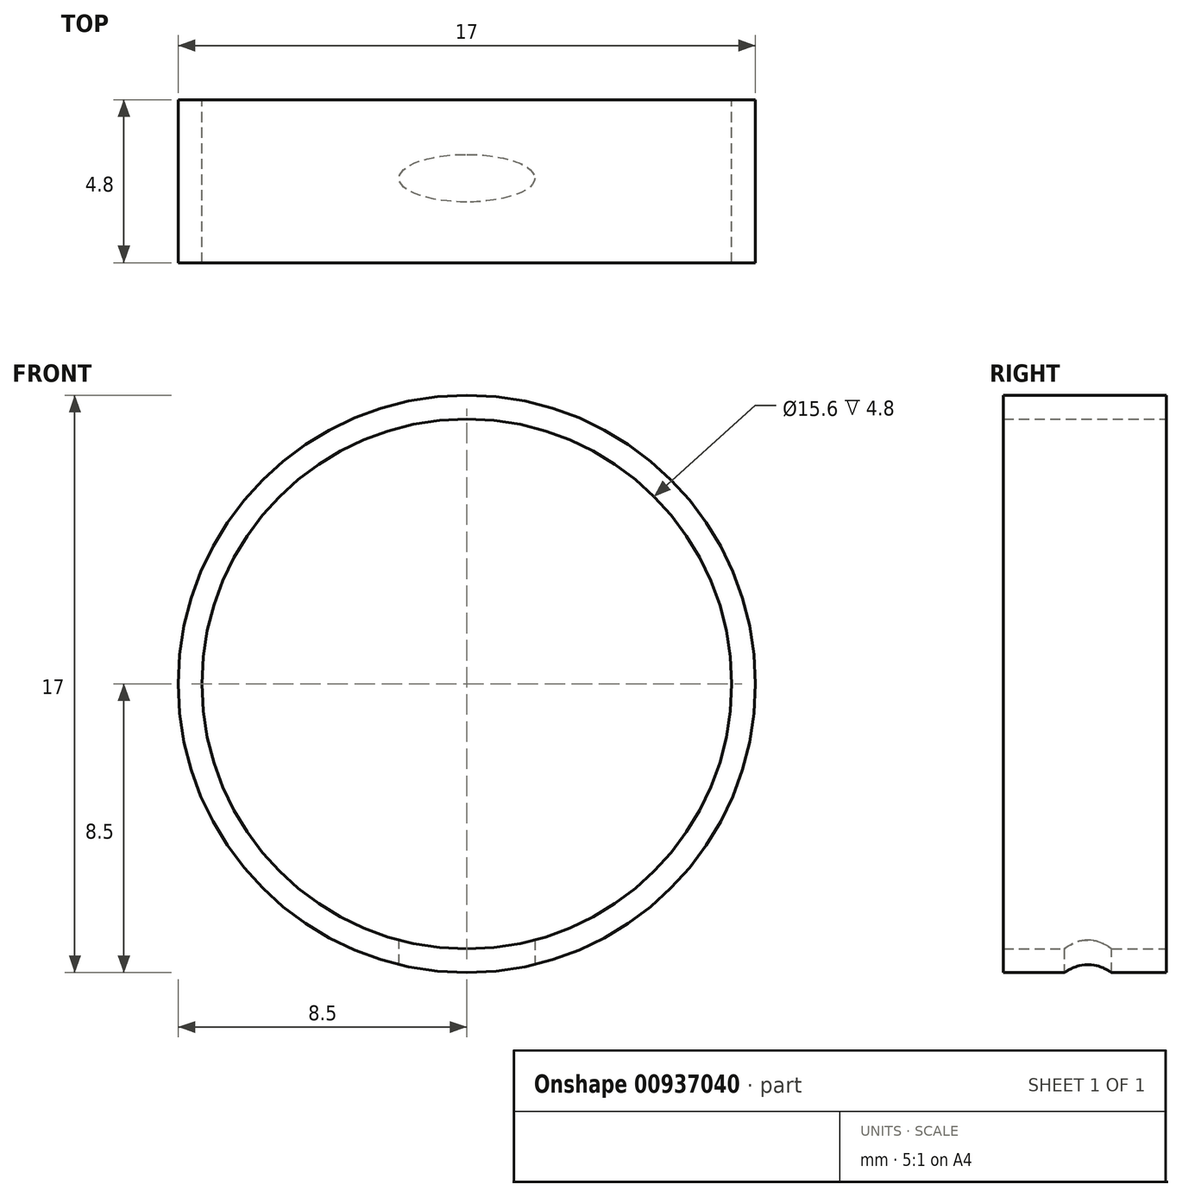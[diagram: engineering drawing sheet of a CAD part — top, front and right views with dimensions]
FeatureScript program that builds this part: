
annotation { "Feature Type Name" : "Feature", "Feature Type Description" : "" }
export const myFeature = defineFeature(function(context is Context, id is Id, definition is map)
    precondition{}
    {
        {
            var Q0;
            Q0=qCreatedBy(makeId("Front.planeOp"),FACE);
            var sketch = newSketch(context, id + "F0", { "sketchPlane" : qUnion([Q0])});
            skCircle(sketch, "E0", {"center": v(0, 0) * mm, "radius": 8.5 * mm});
            skCircle(sketch, "E1", {"center": v(0, 0) * mm, "radius": 7.8 * mm});
            skSolve(sketch);
        }
        {
            var Q0;
            Q0=makeQuery(id+"F0.imprint","IMPRINT",FACE,{"disambiguationData":[TD([[makeQuery(id+"F0.imprint","IMPRINT",EDGE,{"derivedFrom":sQuery(id+"F0.wireOp",EDGE,"E0")}),1.0]])]});
            extrude(context, id + "F1", {"entities" : qUnion([Q0]), "depth" : 4.8 * mm, "offsetDistance" : 25 * mm});
        }
        {
            var Q0;
            Q0=qCreatedBy(makeId("Top.planeOp"),FACE);
            cPlane(context, id + "F2", {"entities" : qUnion([Q0]), "cplaneType" : CPlaneType.OFFSET, "offset" : 9 * mm, "oppositeDirection" : true, "width" : 150 * mm, "height" : 150 * mm});
        }
        {
            var Q0;
            Q0=qCreatedBy(id+"F2.planeOp",FACE);
            var sketch = newSketch(context, id + "F3", { "sketchPlane" : qUnion([Q0])});
            skLineSegment(sketch, "E2.0", {"start": v(8.5, 0) * mm, "end": v(-8.5, 0) * mm});
            skLineSegment(sketch, "E3.0", {"start": v(8.5, -4.8) * mm, "end": v(-8.5, -4.8) * mm});
            skLineSegment(sketch, "E4", {"start": v(8.5, 0) * mm, "end": v(8.5, -4.62) * mm});
            skLineSegment(sketch, "E5", {"start": v(-8.5, -4.62) * mm, "end": v(-8.5, 0) * mm});
            skEllipse(sketch, "E6", {"center": v(0, -2.31) * mm, "majorRadius": 2 * mm, "minorRadius": 0.7 * mm, "majorAxis": v(1, 0)});
            skPoint(sketch, "E6.centerSnap0", {"position": v(-8.5, -2.31) * mm});
            skPoint(sketch, "E6.centerSnap1", {"position": v(0, 0) * mm});
            skSolve(sketch);
        }
        {
            var Q0;
            Q0=makeQuery(id+"F3.imprint","IMPRINT",FACE,{"disambiguationData":[TD([[makeQuery(id+"F3.imprint","IMPRINT",EDGE,{"derivedFrom":sQuery(id+"F3.wireOp",EDGE,"E6")}),1.0]])]});
            extrude(context, id + "F4", {"entities" : qUnion([Q0]), "operationType" : NewBodyOperationType.REMOVE, "depth" : 2 * mm, "offsetDistance" : 25 * mm});
        }
    });
